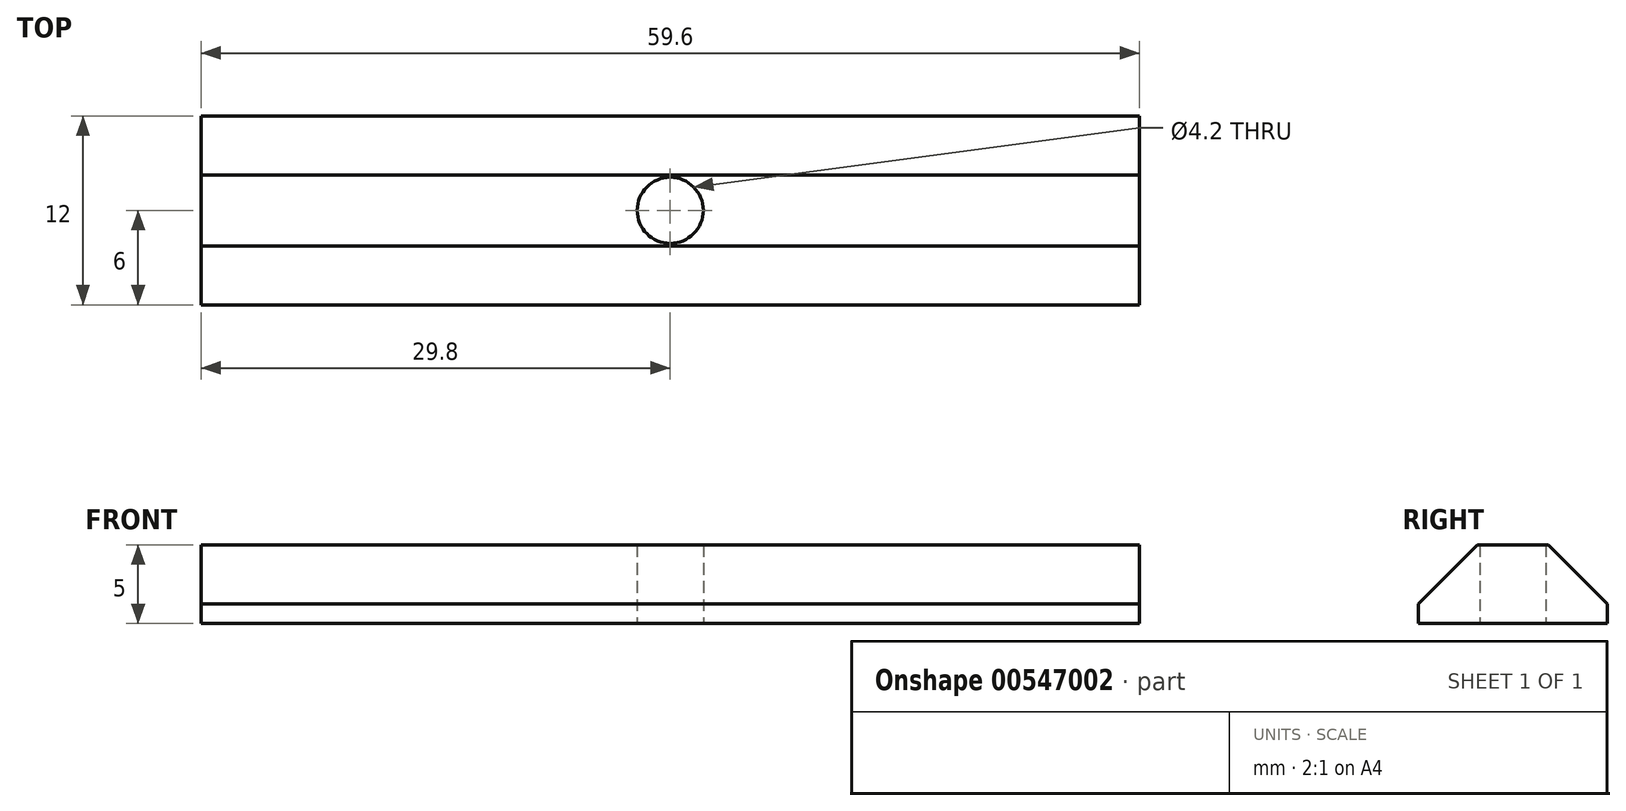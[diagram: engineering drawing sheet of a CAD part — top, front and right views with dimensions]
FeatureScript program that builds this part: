
annotation { "Feature Type Name" : "Feature", "Feature Type Description" : "" }
export const myFeature = defineFeature(function(context is Context, id is Id, definition is map)
    precondition{}
    {
        {
            var Q0;
            Q0=qCreatedBy(makeId("Top.planeOp"),FACE);
            var sketch = newSketch(context, id + "F0", { "sketchPlane" : qUnion([Q0])});
            skLineSegment(sketch, "E0.bottom", {"start": v(29.8, -2.25) * mm, "end": v(-29.8, -2.25) * mm});
            skLineSegment(sketch, "E0.top", {"start": v(29.8, 2.25) * mm, "end": v(-29.8, 2.25) * mm});
            skLineSegment(sketch, "E0.left", {"start": v(29.8, -2.25) * mm, "end": v(29.8, 2.25) * mm});
            skLineSegment(sketch, "E0.right", {"start": v(-29.8, -2.25) * mm, "end": v(-29.8, 2.25) * mm});
            skPoint(sketch, "E0.middle", {"position": v(0, 0) * mm});
            skLineSegment(sketch, "E1.bottom", {"start": v(29.8, -6) * mm, "end": v(-29.8, -6) * mm});
            skLineSegment(sketch, "E1.top", {"start": v(29.8, 6) * mm, "end": v(-29.8, 6) * mm});
            skLineSegment(sketch, "E1.left", {"start": v(29.8, -6) * mm, "end": v(29.8, 6) * mm});
            skLineSegment(sketch, "E1.right", {"start": v(-29.8, -6) * mm, "end": v(-29.8, 6) * mm});
            skCircle(sketch, "E2", {"center": v(0, 0) * mm, "radius": 2.1 * mm});
            skSolve(sketch);
        }
        {
            var Q0;
            {var subQ0=sQuery(id+"F0.wireOp",EDGE,"E0.top");Q0=makeQuery(id+"F0.imprint","IMPRINT",FACE,{"disambiguationData":[TD([[makeQuery(id+"F0.imprint","IMPRINT",EDGE,{"derivedFrom":subQ0}),-1.0]])]});}
            var Q1;
            {var subQ1=sQuery(id+"F0.wireOp",EDGE,"E0.bottom");Q1=makeQuery(id+"F0.imprint","IMPRINT",FACE,{"disambiguationData":[TD([[makeQuery(id+"F0.imprint","IMPRINT",EDGE,{"derivedFrom":subQ1}),-1.0]])]});}
            var Q2;
            {var subQ0=sQuery(id+"F0.wireOp",EDGE,"E0.bottom");Q2=makeQuery(id+"F0.imprint","IMPRINT",FACE,{"disambiguationData":[TD([[makeQuery(id+"F0.imprint","IMPRINT",EDGE,{"derivedFrom":subQ0}),1.0]])]});}
            extrude(context, id + "F1", {"entities" : qUnion([Q0, Q1, Q2]), "depth" : 5 * mm, "offsetDistance" : 25 * mm});
        }
        {
            var Q0;
            Q0=makeQuery(id+"F1.opExtrude","CAP_EDGE",EDGE,{"disambiguationData":[OSD([sQuery(id+"F0.wireOp",EDGE,"E1.bottom")])],"isStart":false});
            var Q1;
            Q1=makeQuery(id+"F1.opExtrude","CAP_EDGE",EDGE,{"disambiguationData":[OSD([sQuery(id+"F0.wireOp",EDGE,"E1.top")])],"isStart":false});
            chamfer(context, id + "F2", {"entities" : qUnion([Q0, Q1]), "width" : 3.75 * mm, "tangentPropagation" : true});
        }
    });
